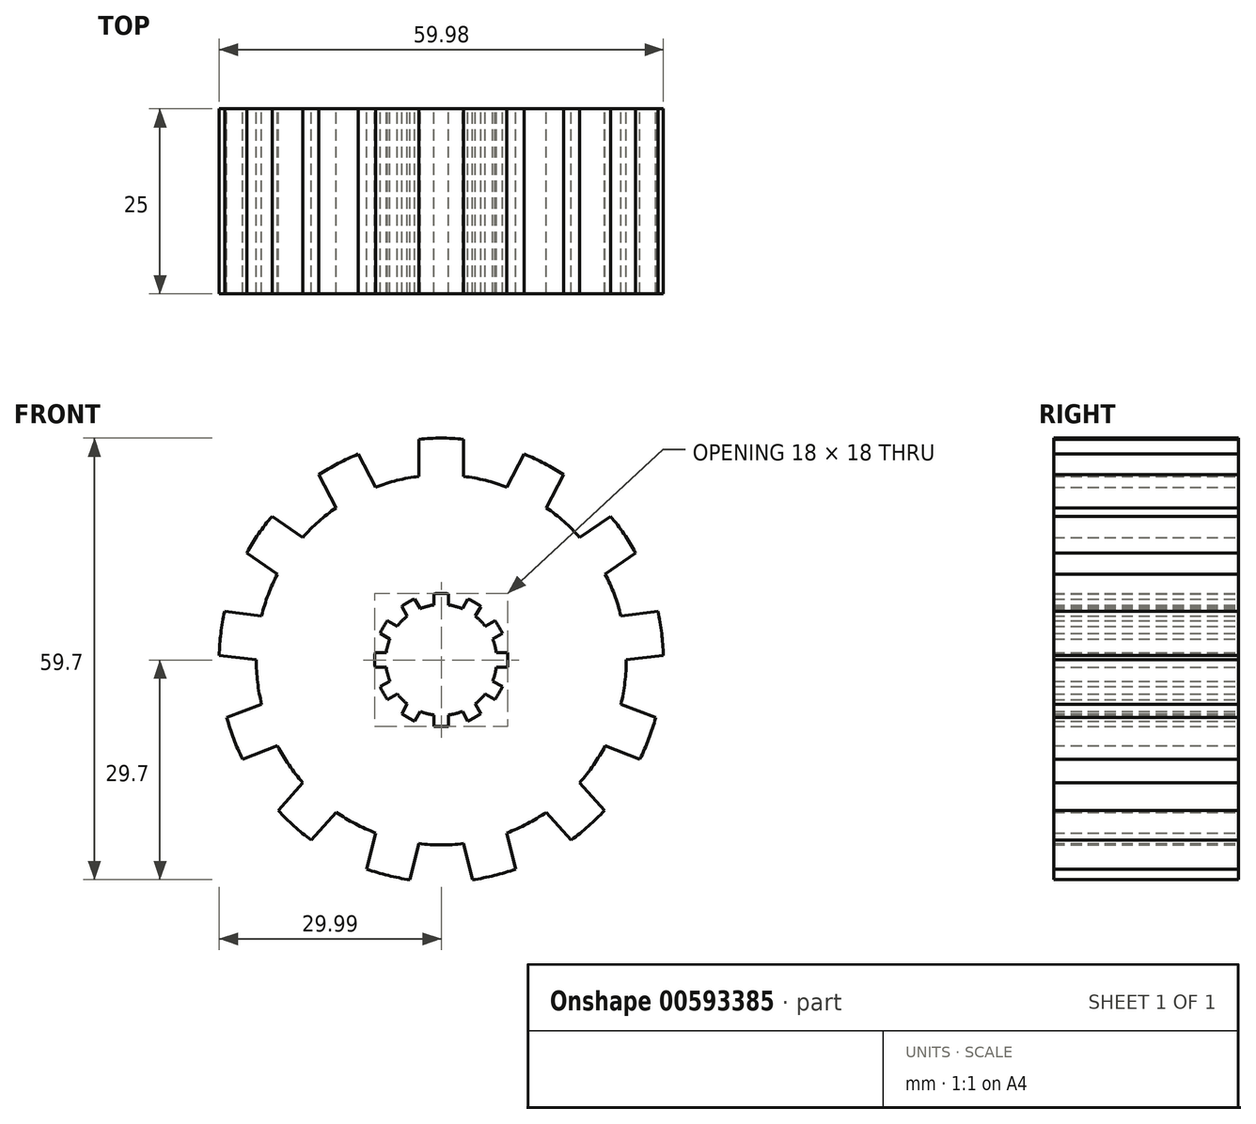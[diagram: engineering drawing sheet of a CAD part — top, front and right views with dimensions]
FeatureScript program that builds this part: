
annotation { "Feature Type Name" : "Feature", "Feature Type Description" : "" }
export const myFeature = defineFeature(function(context is Context, id is Id, definition is map)
    precondition{}
    {
        {
            var Q0;
            Q0=qCreatedBy(makeId("Front.planeOp"),FACE);
            var sketch = newSketch(context, id + "F0", { "sketchPlane" : qUnion([Q0])});
            skArc(sketch, "E0", {"start": v(-4.58, 5.94) * mm, "mid": v(-5.3, 5.3) * mm, "end": v(-5.94, 4.58) * mm});
            skArc(sketch, "E1", {"start": v(1, 8.94) * mm, "mid": v(0, 9) * mm, "end": v(-1, 8.94) * mm});
            skLineSegment(sketch, "E2", {"start": v(-1, 8.94) * mm, "end": v(-1, 7.43) * mm});
            skLineSegment(sketch, "E3", {"start": v(1, 7.43) * mm, "end": v(1, 8.94) * mm});
            skArc(sketch, "E4.1.0", {"start": v(-3.6, 8.25) * mm, "mid": v(-4.5, 7.8) * mm, "end": v(-5.34, 7.25) * mm});
            skLineSegment(sketch, "E4.1.1", {"start": v(-2.85, 6.94) * mm, "end": v(-3.6, 8.25) * mm});
            skLineSegment(sketch, "E4.1.2", {"start": v(-5.34, 7.25) * mm, "end": v(-4.58, 5.94) * mm});
            skArc(sketch, "E4.2.0", {"start": v(-7.25, 5.34) * mm, "mid": v(-7.8, 4.5) * mm, "end": v(-8.25, 3.6) * mm});
            skLineSegment(sketch, "E4.2.1", {"start": v(-5.94, 4.58) * mm, "end": v(-7.25, 5.34) * mm});
            skLineSegment(sketch, "E4.2.2", {"start": v(-8.25, 3.6) * mm, "end": v(-6.94, 2.85) * mm});
            skArc(sketch, "E4.3.0", {"start": v(-8.94, 1) * mm, "mid": v(-9, 0) * mm, "end": v(-8.94, -1) * mm});
            skLineSegment(sketch, "E4.3.1", {"start": v(-7.43, 1) * mm, "end": v(-8.94, 1) * mm});
            skLineSegment(sketch, "E4.3.2", {"start": v(-8.94, -1) * mm, "end": v(-7.43, -1) * mm});
            skArc(sketch, "E4.4.0", {"start": v(-8.25, -3.6) * mm, "mid": v(-7.8, -4.5) * mm, "end": v(-7.25, -5.34) * mm});
            skLineSegment(sketch, "E4.4.1", {"start": v(-6.94, -2.85) * mm, "end": v(-8.25, -3.6) * mm});
            skLineSegment(sketch, "E4.4.2", {"start": v(-7.25, -5.34) * mm, "end": v(-5.94, -4.58) * mm});
            skArc(sketch, "E4.5.0", {"start": v(-5.34, -7.25) * mm, "mid": v(-4.5, -7.8) * mm, "end": v(-3.6, -8.25) * mm});
            skLineSegment(sketch, "E4.5.1", {"start": v(-4.58, -5.94) * mm, "end": v(-5.34, -7.25) * mm});
            skLineSegment(sketch, "E4.5.2", {"start": v(-3.6, -8.25) * mm, "end": v(-2.85, -6.94) * mm});
            skArc(sketch, "E4.6.0", {"start": v(-1, -8.94) * mm, "mid": v(0, -9) * mm, "end": v(1, -8.94) * mm});
            skLineSegment(sketch, "E4.6.1", {"start": v(-1, -7.43) * mm, "end": v(-1, -8.94) * mm});
            skLineSegment(sketch, "E4.6.2", {"start": v(1, -8.94) * mm, "end": v(1, -7.43) * mm});
            skArc(sketch, "E4.7.0", {"start": v(3.6, -8.25) * mm, "mid": v(4.5, -7.8) * mm, "end": v(5.34, -7.25) * mm});
            skLineSegment(sketch, "E4.7.1", {"start": v(2.85, -6.94) * mm, "end": v(3.6, -8.25) * mm});
            skLineSegment(sketch, "E4.7.2", {"start": v(5.34, -7.25) * mm, "end": v(4.58, -5.94) * mm});
            skArc(sketch, "E4.8.0", {"start": v(7.25, -5.34) * mm, "mid": v(7.8, -4.5) * mm, "end": v(8.25, -3.6) * mm});
            skLineSegment(sketch, "E4.8.1", {"start": v(5.94, -4.58) * mm, "end": v(7.25, -5.34) * mm});
            skLineSegment(sketch, "E4.8.2", {"start": v(8.25, -3.6) * mm, "end": v(6.94, -2.85) * mm});
            skArc(sketch, "E4.9.0", {"start": v(8.94, -1) * mm, "mid": v(9, 0) * mm, "end": v(8.94, 1) * mm});
            skLineSegment(sketch, "E4.9.1", {"start": v(7.43, -1) * mm, "end": v(8.94, -1) * mm});
            skLineSegment(sketch, "E4.9.2", {"start": v(8.94, 1) * mm, "end": v(7.43, 1) * mm});
            skArc(sketch, "E4.10.0", {"start": v(8.25, 3.6) * mm, "mid": v(7.8, 4.5) * mm, "end": v(7.25, 5.34) * mm});
            skLineSegment(sketch, "E4.10.1", {"start": v(6.94, 2.85) * mm, "end": v(8.25, 3.6) * mm});
            skLineSegment(sketch, "E4.10.2", {"start": v(7.25, 5.34) * mm, "end": v(5.94, 4.58) * mm});
            skArc(sketch, "E4.11.0", {"start": v(5.34, 7.25) * mm, "mid": v(4.5, 7.8) * mm, "end": v(3.6, 8.25) * mm});
            skLineSegment(sketch, "E4.11.1", {"start": v(4.58, 5.94) * mm, "end": v(5.34, 7.25) * mm});
            skLineSegment(sketch, "E4.11.2", {"start": v(3.6, 8.25) * mm, "end": v(2.85, 6.94) * mm});
            skArc(sketch, "E5.trimOffspring", {"start": v(-1, 7.43) * mm, "mid": v(-1.94, 7.24) * mm, "end": v(-2.85, 6.94) * mm});
            skArc(sketch, "E6.trimOffspring", {"start": v(2.85, 6.94) * mm, "mid": v(1.94, 7.24) * mm, "end": v(1, 7.43) * mm});
            skArc(sketch, "E7.trimOffspring", {"start": v(5.94, 4.58) * mm, "mid": v(5.3, 5.3) * mm, "end": v(4.58, 5.94) * mm});
            skArc(sketch, "E8.trimOffspring", {"start": v(7.43, 1) * mm, "mid": v(7.24, 1.94) * mm, "end": v(6.94, 2.85) * mm});
            skArc(sketch, "E9.trimOffspring", {"start": v(6.94, -2.85) * mm, "mid": v(7.24, -1.94) * mm, "end": v(7.43, -1) * mm});
            skArc(sketch, "E10.trimOffspring", {"start": v(4.58, -5.94) * mm, "mid": v(5.3, -5.3) * mm, "end": v(5.94, -4.58) * mm});
            skArc(sketch, "E11.trimOffspring", {"start": v(1, -7.43) * mm, "mid": v(1.94, -7.24) * mm, "end": v(2.85, -6.94) * mm});
            skArc(sketch, "E12.trimOffspring", {"start": v(-2.85, -6.94) * mm, "mid": v(-1.94, -7.24) * mm, "end": v(-1, -7.43) * mm});
            skArc(sketch, "E13.trimOffspring", {"start": v(-5.94, -4.58) * mm, "mid": v(-5.3, -5.3) * mm, "end": v(-4.58, -5.94) * mm});
            skArc(sketch, "E14.trimOffspring", {"start": v(-7.43, -1) * mm, "mid": v(-7.24, -1.94) * mm, "end": v(-6.94, -2.85) * mm});
            skArc(sketch, "E15.trimOffspring", {"start": v(-6.94, 2.85) * mm, "mid": v(-7.24, 1.94) * mm, "end": v(-7.43, 1) * mm});
            skArc(sketch, "E16", {"start": v(-14.2, 20.58) * mm, "mid": v(-16.58, 18.71) * mm, "end": v(-18.72, 16.57) * mm});
            skLineSegment(sketch, "E17", {"start": v(-3, 29.85) * mm, "end": v(-3, 24.82) * mm});
            skLineSegment(sketch, "E18", {"start": v(3, 24.82) * mm, "end": v(3, 29.85) * mm});
            skArc(sketch, "E19", {"start": v(3, 29.85) * mm, "mid": v(0, 30) * mm, "end": v(-3, 29.85) * mm});
            skLineSegment(sketch, "E20.1.0", {"start": v(-16.53, 25.04) * mm, "end": v(-14.2, 20.58) * mm});
            skArc(sketch, "E20.1.1", {"start": v(-11.22, 27.82) * mm, "mid": v(-13.94, 26.56) * mm, "end": v(-16.53, 25.04) * mm});
            skLineSegment(sketch, "E20.1.2", {"start": v(-8.88, 23.37) * mm, "end": v(-11.22, 27.82) * mm});
            skLineSegment(sketch, "E20.2.0", {"start": v(-26.27, 14.49) * mm, "end": v(-22.13, 11.63) * mm});
            skArc(sketch, "E20.2.1", {"start": v(-22.86, 19.43) * mm, "mid": v(-24.69, 17.04) * mm, "end": v(-26.27, 14.49) * mm});
            skLineSegment(sketch, "E20.2.2", {"start": v(-18.72, 16.57) * mm, "end": v(-22.86, 19.43) * mm});
            skLineSegment(sketch, "E20.3.0", {"start": v(-30, 0.62) * mm, "end": v(-25, 0.01) * mm});
            skArc(sketch, "E20.3.1", {"start": v(-29.27, 6.58) * mm, "mid": v(-29.78, 3.62) * mm, "end": v(-30, 0.62) * mm});
            skLineSegment(sketch, "E20.3.2", {"start": v(-24.28, 5.97) * mm, "end": v(-29.27, 6.58) * mm});
            skLineSegment(sketch, "E20.4.0", {"start": v(-26.85, -13.39) * mm, "end": v(-22.14, -11.6) * mm});
            skArc(sketch, "E20.4.1", {"start": v(-28.97, -7.78) * mm, "mid": v(-28.05, -10.64) * mm, "end": v(-26.85, -13.39) * mm});
            skLineSegment(sketch, "E20.4.2", {"start": v(-24.27, -6) * mm, "end": v(-28.97, -7.78) * mm});
            skLineSegment(sketch, "E20.5.0", {"start": v(-17.55, -24.33) * mm, "end": v(-14.21, -20.57) * mm});
            skArc(sketch, "E20.5.1", {"start": v(-22.04, -20.35) * mm, "mid": v(-19.9, -22.46) * mm, "end": v(-17.55, -24.33) * mm});
            skLineSegment(sketch, "E20.5.2", {"start": v(-18.7, -16.59) * mm, "end": v(-22.04, -20.35) * mm});
            skLineSegment(sketch, "E20.6.0", {"start": v(-4.23, -29.7) * mm, "end": v(-3.03, -24.82) * mm});
            skArc(sketch, "E20.6.1", {"start": v(-10.06, -28.26) * mm, "mid": v(-7.18, -29.13) * mm, "end": v(-4.23, -29.7) * mm});
            skLineSegment(sketch, "E20.6.2", {"start": v(-8.85, -23.38) * mm, "end": v(-10.06, -28.26) * mm});
            skLineSegment(sketch, "E20.7.0", {"start": v(10.06, -28.26) * mm, "end": v(8.85, -23.38) * mm});
            skArc(sketch, "E20.7.1", {"start": v(4.23, -29.7) * mm, "mid": v(7.18, -29.13) * mm, "end": v(10.06, -28.26) * mm});
            skLineSegment(sketch, "E20.7.2", {"start": v(3.03, -24.82) * mm, "end": v(4.23, -29.7) * mm});
            skLineSegment(sketch, "E20.8.0", {"start": v(22.04, -20.35) * mm, "end": v(18.7, -16.59) * mm});
            skArc(sketch, "E20.8.1", {"start": v(17.55, -24.33) * mm, "mid": v(19.9, -22.46) * mm, "end": v(22.04, -20.35) * mm});
            skLineSegment(sketch, "E20.8.2", {"start": v(14.21, -20.57) * mm, "end": v(17.55, -24.33) * mm});
            skLineSegment(sketch, "E20.9.0", {"start": v(28.97, -7.78) * mm, "end": v(24.27, -6) * mm});
            skArc(sketch, "E20.9.1", {"start": v(26.85, -13.39) * mm, "mid": v(28.05, -10.64) * mm, "end": v(28.97, -7.78) * mm});
            skLineSegment(sketch, "E20.9.2", {"start": v(22.14, -11.6) * mm, "end": v(26.85, -13.39) * mm});
            skLineSegment(sketch, "E20.10.0", {"start": v(29.27, 6.58) * mm, "end": v(24.28, 5.97) * mm});
            skArc(sketch, "E20.10.1", {"start": v(30, 0.62) * mm, "mid": v(29.78, 3.62) * mm, "end": v(29.27, 6.58) * mm});
            skLineSegment(sketch, "E20.10.2", {"start": v(25, 0.01) * mm, "end": v(30, 0.62) * mm});
            skLineSegment(sketch, "E20.11.0", {"start": v(22.86, 19.43) * mm, "end": v(18.72, 16.57) * mm});
            skArc(sketch, "E20.11.1", {"start": v(26.27, 14.49) * mm, "mid": v(24.69, 17.04) * mm, "end": v(22.86, 19.43) * mm});
            skLineSegment(sketch, "E20.11.2", {"start": v(22.13, 11.63) * mm, "end": v(26.27, 14.49) * mm});
            skLineSegment(sketch, "E20.12.0", {"start": v(11.22, 27.82) * mm, "end": v(8.88, 23.37) * mm});
            skArc(sketch, "E20.12.1", {"start": v(16.53, 25.04) * mm, "mid": v(13.94, 26.56) * mm, "end": v(11.22, 27.82) * mm});
            skLineSegment(sketch, "E20.12.2", {"start": v(14.2, 20.58) * mm, "end": v(16.53, 25.04) * mm});
            skArc(sketch, "E21.trimOffspring", {"start": v(8.88, 23.37) * mm, "mid": v(5.98, 24.27) * mm, "end": v(3, 24.82) * mm});
            skArc(sketch, "E22.trimOffspring", {"start": v(-3, 24.82) * mm, "mid": v(-5.98, 24.27) * mm, "end": v(-8.88, 23.37) * mm});
            skArc(sketch, "E23.trimOffspring", {"start": v(18.72, 16.57) * mm, "mid": v(16.58, 18.71) * mm, "end": v(14.2, 20.58) * mm});
            skArc(sketch, "E24.trimOffspring", {"start": v(24.28, 5.97) * mm, "mid": v(23.38, 8.87) * mm, "end": v(22.13, 11.63) * mm});
            skArc(sketch, "E25.trimOffspring", {"start": v(24.27, -6) * mm, "mid": v(24.82, -3.01) * mm, "end": v(25, 0.01) * mm});
            skArc(sketch, "E26.trimOffspring", {"start": v(18.7, -16.59) * mm, "mid": v(20.57, -14.2) * mm, "end": v(22.14, -11.6) * mm});
            skArc(sketch, "E27.trimOffspring", {"start": v(8.85, -23.38) * mm, "mid": v(11.62, -22.14) * mm, "end": v(14.21, -20.57) * mm});
            skArc(sketch, "E28.trimOffspring", {"start": v(-3.03, -24.82) * mm, "mid": v(0, -25) * mm, "end": v(3.03, -24.82) * mm});
            skArc(sketch, "E29.trimOffspring", {"start": v(-14.21, -20.57) * mm, "mid": v(-11.62, -22.14) * mm, "end": v(-8.85, -23.38) * mm});
            skArc(sketch, "E30.trimOffspring", {"start": v(-22.14, -11.6) * mm, "mid": v(-20.57, -14.2) * mm, "end": v(-18.7, -16.59) * mm});
            skArc(sketch, "E31.trimOffspring", {"start": v(-25, 0.01) * mm, "mid": v(-24.82, -3.01) * mm, "end": v(-24.27, -6) * mm});
            skArc(sketch, "E32.trimOffspring", {"start": v(-22.13, 11.63) * mm, "mid": v(-23.38, 8.87) * mm, "end": v(-24.28, 5.97) * mm});
            skSolve(sketch);
        }
        {
            var Q0;
            Q0=makeQuery(id+"F0.imprint","IMPRINT",FACE,{"disambiguationData":[TD([[makeQuery(id+"F0.imprint","IMPRINT",EDGE,{"derivedFrom":sQuery(id+"F0.wireOp",EDGE,"E0")}),-1.0]])]});
            extrude(context, id + "F1", {"entities" : qUnion([Q0]), "depth" : 25 * mm, "offsetDistance" : 25 * mm});
        }
    });
